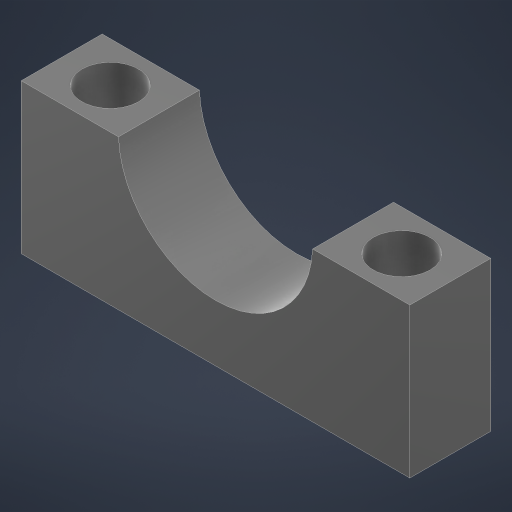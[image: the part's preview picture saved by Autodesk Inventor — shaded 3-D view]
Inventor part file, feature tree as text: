
AUTODESK INVENTOR PART (.ipt)
format: ipt  version: 2025 (Build 290162010, 162A)  size: 187,392 bytes
history: native  units: mm
features: extrude x2
ambient origin geometry x8: Origin, YZ Plane, XZ Plane, XY Plane, X Axis, Y Axis, Z Axis, Center Point
bodies: Solid1 (feature_tree)
feature tree (2):
  extrude  "Extrusion1"  Depth=12.0mm
  extrude  "Extrusion2"  Depth=24.0mm
